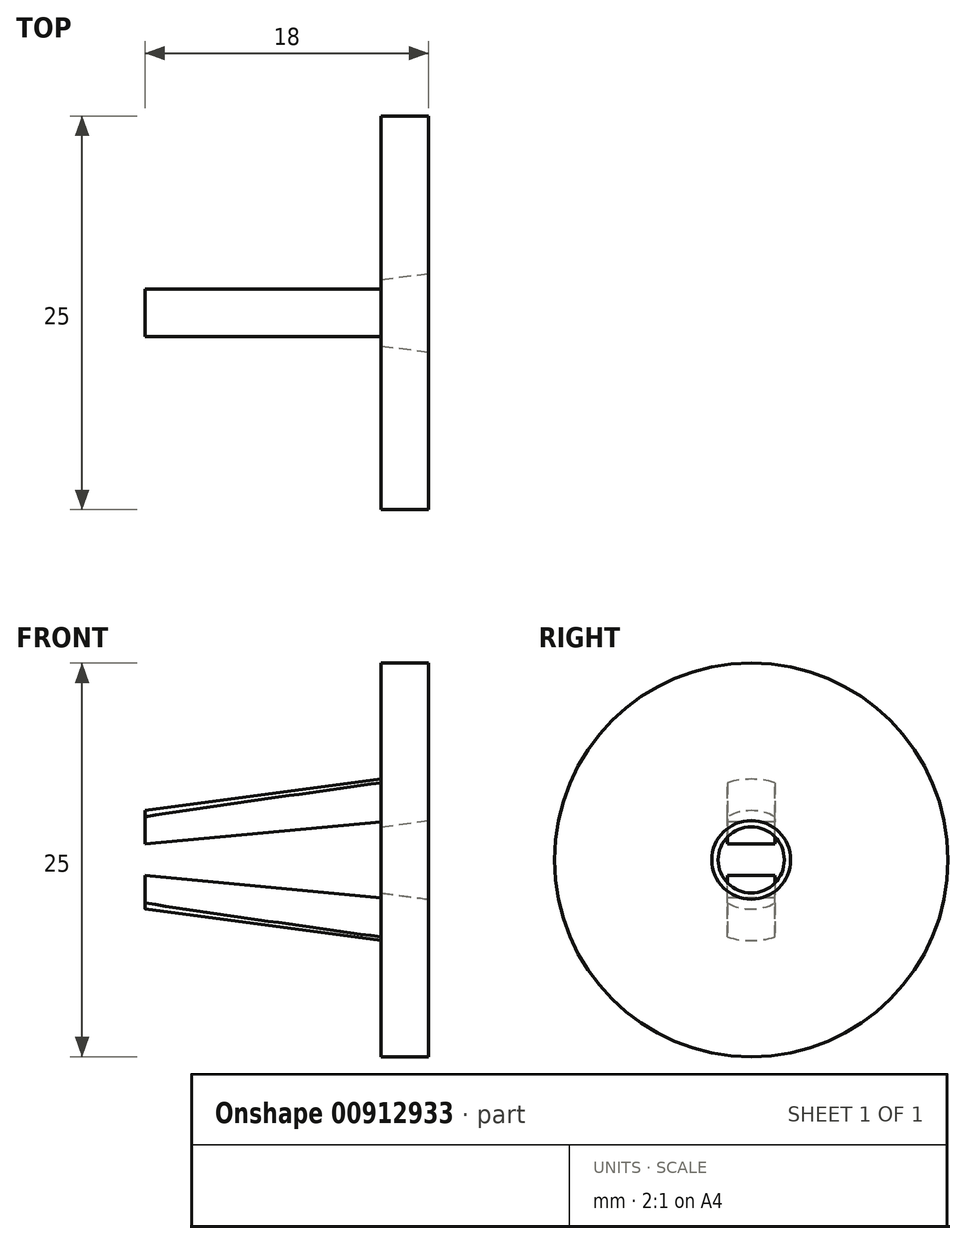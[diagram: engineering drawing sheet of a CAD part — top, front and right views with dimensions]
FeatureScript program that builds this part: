
annotation { "Feature Type Name" : "Feature", "Feature Type Description" : "" }
export const myFeature = defineFeature(function(context is Context, id is Id, definition is map)
    precondition{}
    {
        {
            var Q0;
            Q0=qCreatedBy(makeId("Front.planeOp"),FACE);
            var sketch = newSketch(context, id + "F0", { "sketchPlane" : qUnion([Q0])});
            skLineSegment(sketch, "E0", {"start": v(-18, 0.1) * mm, "end": v(-18, 3.13) * mm});
            skLineSegment(sketch, "E1", {"start": v(-18, 3.13) * mm, "end": v(-3, 5.13) * mm});
            skLineSegment(sketch, "E2", {"start": v(-3, 5.13) * mm, "end": v(-3, 12.5) * mm});
            skLineSegment(sketch, "E3", {"start": v(-3, 12.5) * mm, "end": v(0, 12.5) * mm});
            skLineSegment(sketch, "E4", {"start": v(0, 12.5) * mm, "end": v(0, 2.5) * mm});
            skLineSegment(sketch, "E5", {"start": v(-18, 0.1) * mm, "end": v(0, 2.5) * mm});
            skLineSegment(sketch, "E6", {"start": v(0, 0) * mm, "end": v(-15.96, 0) * mm, "construction": true});
            skSolve(sketch);
        }
        {
            var Q0;
            Q0=qCreatedBy(makeId("Front.planeOp"),FACE);
            var sketch = newSketch(context, id + "F1", { "sketchPlane" : qUnion([Q0])});
            skLineSegment(sketch, "E7", {"start": v(0, 0) * mm, "end": v(-17.67, 0) * mm, "construction": true});
            skSolve(sketch);
        }
        {
            var Q0;
            Q0 = qSketchRegion(id + "F0", true);
            var Q1;
            Q1=sQuery(id+"F1.wireOp",EDGE,"E7");
            revolve(context, id + "F2", {"surfaceOperationType" : NewSurfaceOperationType.NEW, "entities" : qUnion([Q0]), "axis" : qUnion([Q1]), "revolveType" : RevolveType.FULL});
        }
        {
            var Q0;
            Q0=qCreatedBy(makeId("Top.planeOp"),FACE);
            var sketch = newSketch(context, id + "F3", { "sketchPlane" : qUnion([Q0])});
            skLineSegment(sketch, "E8.bottom", {"start": v(-23, 1.5) * mm, "end": v(-3, 1.5) * mm});
            skLineSegment(sketch, "E8.top", {"start": v(-23, 6.07) * mm, "end": v(-3, 6.07) * mm});
            skLineSegment(sketch, "E8.left", {"start": v(-23, 1.5) * mm, "end": v(-23, 6.07) * mm});
            skLineSegment(sketch, "E8.right", {"start": v(-3, 1.5) * mm, "end": v(-3, 6.07) * mm});
            skLineSegment(sketch, "E9", {"start": v(0, 0) * mm, "end": v(-11.43, 0) * mm, "construction": true});
            skLineSegment(sketch, "E10.MirrorCS", {"start": v(-23, -1.5) * mm, "end": v(-23, -6.07) * mm});
            skLineSegment(sketch, "E11.MirrorCS", {"start": v(-23, -6.07) * mm, "end": v(-3, -6.07) * mm});
            skLineSegment(sketch, "E12.MirrorCS", {"start": v(-23, -1.5) * mm, "end": v(-3, -1.5) * mm});
            skLineSegment(sketch, "E13", {"start": v(-3, -1.5) * mm, "end": v(-3, -6.07) * mm});
            skSolve(sketch);
        }
        {
            var Q0;
            Q0 = qSketchRegion(id + "F3", true);
            extrude(context, id + "F4", {"entities" : qUnion([Q0]), "operationType" : NewBodyOperationType.REMOVE, "endBound" : BoundingType.THROUGH_ALL, "depth" : 25 * mm, "offsetDistance" : 25 * mm});
        }
        {
            var Q0;
            Q0 = qSketchRegion(id + "F3", true);
            extrude(context, id + "F5", {"entities" : qUnion([Q0]), "operationType" : NewBodyOperationType.REMOVE, "oppositeDirection" : true, "depth" : 25 * mm, "offsetDistance" : 25 * mm});
        }
        {
            var Q0;
            {var subQ0=sQuery(id+"F3.wireOp",EDGE,"E12.MirrorCS");Q0=makeQuery(id+"F5.boolean.opBoolean","MERGE",FACE,{"derivedFrom":[makeQuery(id+"F4.boolean.opBoolean","COPY",FACE,{"derivedFrom":makeQuery(id+"F4.opExtrude","SWEPT_FACE",FACE,{"disambiguationData":[OSD([subQ0])]})})],"fromTools":[makeQuery(id+"F5.opExtrude","SWEPT_FACE",FACE,{"disambiguationData":[OSD([subQ0])]})]});}
            var sketch = newSketch(context, id + "F6", { "sketchPlane" : qUnion([Q0])});
            skLineSegment(sketch, "E14", {"start": v(-3, 2.4) * mm, "end": v(-18, 1) * mm});
            skLineSegment(sketch, "E15", {"start": v(-18, 1) * mm, "end": v(-18, 0) * mm});
            skLineSegment(sketch, "E16", {"start": v(-3, 2.4) * mm, "end": v(-3, 0) * mm});
            skLineSegment(sketch, "E17.MirrorCS", {"start": v(-3, -2.4) * mm, "end": v(-18, -1) * mm});
            skLineSegment(sketch, "E18.MirrorCS", {"start": v(-18, -1) * mm, "end": v(-18, 0) * mm});
            skLineSegment(sketch, "E19.MirrorCS", {"start": v(-3, -2.4) * mm, "end": v(-3, 0) * mm});
            skFitSpline(sketch, "E20.0", {"points": [v(-17.25, 1.83) * mm, v(-15.88, 2.16) * mm, v(-13.13, 2.75) * mm, v(-9, 3.6) * mm, v(-4.86, 4.4) * mm, v(0.66, 5.47) * mm, v(7.56, 6.79) * mm, v(13.09, 7.83) * mm, v(15.85, 8.34) * mm]});
            skSolve(sketch);
        }
        {
            var Q0;
            Q0 = qSketchRegion(id + "F6", true);
            extrude(context, id + "F7", {"entities" : qUnion([Q0]), "operationType" : NewBodyOperationType.REMOVE, "endBound" : BoundingType.THROUGH_ALL, "oppositeDirection" : true, "depth" : 25 * mm, "offsetDistance" : 25 * mm});
        }
    });
